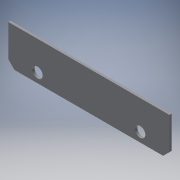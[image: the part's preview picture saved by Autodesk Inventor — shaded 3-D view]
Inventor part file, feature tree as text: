
AUTODESK INVENTOR PART (.ipt)
format: ipt  version: 2017 (Build 210142000, 142)  size: 122,368 bytes
history: native  units: in
note: dims shown in document units (in); Inventor stores cm internally (conversion verified against a paired STEP export)
features: extrude x3, sketch x3, thicken_offset x1
ambient origin geometry x8: Origin, YZ Plane, XZ Plane, XY Plane, X Axis, Y Axis, Z Axis, Center Point
bodies: Solid1 (feature_tree)
feature tree (7):
  extrude  "Extrusion1"  Depth=5.0in
  extrude  "Extrusion2"  Depth=0.25in TaperAngle=0.0deg
  sketch  "Sketch3"  dims[d10=1.124in d14=2.0in d15=0.0in d18=1.124in d19=1.5in d20=180.0deg d31=1.7in d32=1.7in d35=0.82in d36=0.82in]
  extrude  "Extrusion3"  Depth=0.82in TaperAngle=0.0deg
  thicken_offset  "Thicken1"
  sketch  "Sketch1"  dims[d0=17.5in d1=5.0in]
  sketch  "Sketch2"  dims[d2=0.25in d3=0.0in d4=2.0in d5=0.0in]
